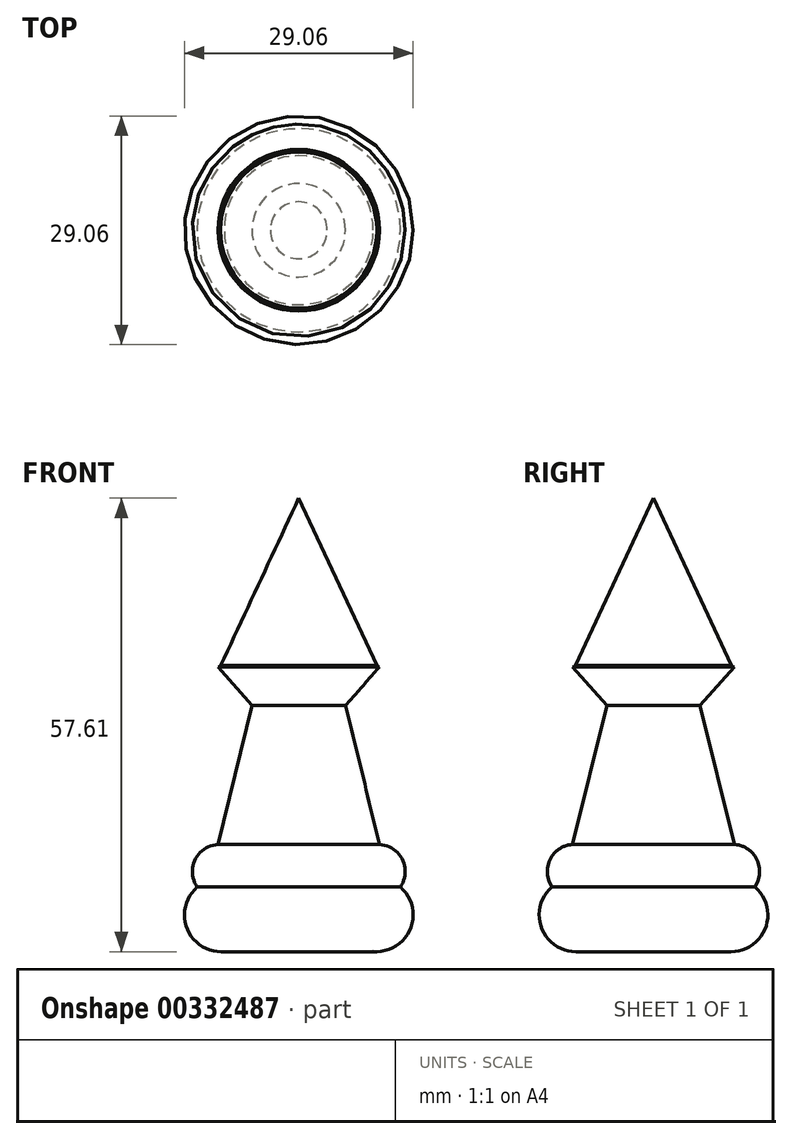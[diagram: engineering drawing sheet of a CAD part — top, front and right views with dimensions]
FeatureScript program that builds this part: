
annotation { "Feature Type Name" : "Feature", "Feature Type Description" : "" }
export const myFeature = defineFeature(function(context is Context, id is Id, definition is map)
    precondition{}
    {
        {
            var Q0;
            Q0=qCreatedBy(makeId("Front.planeOp"),FACE);
            var sketch = newSketch(context, id + "F0", { "sketchPlane" : qUnion([Q0])});
            skLineSegment(sketch, "E0", {"start": v(0, -70.9) * mm, "end": v(-10.27, -70.9) * mm});
            skCircle(sketch, "E1", {"center": v(-9.87, -66.25) * mm, "radius": 4.66 * mm});
            skPoint(sketch, "E1.second.point", {"position": v(-13.74, -63.66) * mm});
            skPoint(sketch, "E1.third.point", {"position": v(-7.09, -62.5) * mm});
            skCircle(sketch, "E2", {"center": v(-10.06, -60.74) * mm, "radius": 3.45 * mm});
            skPoint(sketch, "E2.second.point", {"position": v(-10.27, -57.3) * mm});
            skPoint(sketch, "E2.third.point", {"position": v(-12.88, -58.74) * mm});
            skLineSegment(sketch, "E3", {"start": v(-10.27, -57.3) * mm, "end": v(-5.93, -39.64) * mm});
            skLineSegment(sketch, "E4", {"start": v(-5.93, -39.64) * mm, "end": v(-10.27, -34.72) * mm});
            skLineSegment(sketch, "E5", {"start": v(-10.27, -34.72) * mm, "end": v(0, -34.72) * mm});
            skLineSegment(sketch, "E6", {"start": v(0, -34.72) * mm, "end": v(0, -70.9) * mm});
            skSolve(sketch);
        }
        {
            var Q0;
            {var subQ0=sQuery(id+"F0.wireOp",EDGE,"E1");var subQ1=sQuery(id+"F0.wireOp",EDGE,"E0");var subQ2=makeQuery(id+"F0.imprint","INTERSECT",VERTEX,{"disambiguationData":[OD(0.0)],"derivedFrom":[subQ1,subQ0]});Q0=makeQuery(id+"F0.imprint","IMPRINT",FACE,{"disambiguationData":[TD([[makeQuery(id+"F0.imprint","IMPRINT",EDGE,{"disambiguationData":[TD([[subQ2,1.0]])],"derivedFrom":subQ1}),1.0]])]});}
            var Q1;
            {var subQ0=sQuery(id+"F0.wireOp",EDGE,"E2");var subQ1=sQuery(id+"F0.wireOp",EDGE,"E1");var subQ2=makeQuery(id+"F0.imprint","INTERSECT",VERTEX,{"disambiguationData":[OD(0.0)],"derivedFrom":[subQ1,subQ0]});Q1=makeQuery(id+"F0.imprint","IMPRINT",FACE,{"disambiguationData":[TD([[makeQuery(id+"F0.imprint","IMPRINT",EDGE,{"disambiguationData":[TD([[subQ2,1.0]])],"derivedFrom":subQ1}),-1.0]])]});}
            var Q2;
            {var subQ0=sQuery(id+"F0.wireOp",EDGE,"E2");var subQ1=sQuery(id+"F0.wireOp",EDGE,"E1");var subQ2=makeQuery(id+"F0.imprint","INTERSECT",VERTEX,{"disambiguationData":[OD(0.0)],"derivedFrom":[subQ1,subQ0]});Q2=makeQuery(id+"F0.imprint","IMPRINT",FACE,{"disambiguationData":[TD([[makeQuery(id+"F0.imprint","IMPRINT",EDGE,{"disambiguationData":[TD([[subQ2,1.0]])],"derivedFrom":subQ1}),1.0]])]});}
            var Q3;
            {var subQ0=sQuery(id+"F0.wireOp",EDGE,"E1");var subQ1=sQuery(id+"F0.wireOp",EDGE,"E0");var subQ2=makeQuery(id+"F0.imprint","INTERSECT",VERTEX,{"disambiguationData":[OD(0.0)],"derivedFrom":[subQ1,subQ0]});Q3=makeQuery(id+"F0.imprint","IMPRINT",FACE,{"disambiguationData":[TD([[makeQuery(id+"F0.imprint","IMPRINT",EDGE,{"disambiguationData":[TD([[subQ2,1.0]])],"derivedFrom":subQ1}),-1.0]])]});}
            var Q4;
            {var subQ0=sQuery(id+"F0.wireOp",EDGE,"E3");Q4=makeQuery(id+"F0.imprint","IMPRINT",FACE,{"disambiguationData":[TD([[makeQuery(id+"F0.imprint","IMPRINT",EDGE,{"derivedFrom":subQ0}),-1.0]])]});}
            var Q5;
            Q5=sQuery(id+"F0.wireOp",EDGE,"E6");
            revolve(context, id + "F1", {"entities" : qUnion([Q0, Q1, Q2, Q3, Q4]), "axis" : qUnion([Q5]), "revolveType" : RevolveType.FULL});
        }
        {
            var Q0;
            Q0=qCreatedBy(makeId("Front.planeOp"),FACE);
            var sketch = newSketch(context, id + "F2", { "sketchPlane" : qUnion([Q0])});
            skLineSegment(sketch, "E7", {"start": v(-9.91, -34.59) * mm, "end": v(0, -13.3) * mm});
            skLineSegment(sketch, "E8", {"start": v(0, -13.3) * mm, "end": v(0, -34.8) * mm});
            skLineSegment(sketch, "E9", {"start": v(0, -34.8) * mm, "end": v(-9.91, -34.59) * mm});
            skSolve(sketch);
        }
        {
            var Q0;
            Q0=makeQuery(id+"F2.imprint","IMPRINT",FACE,{"disambiguationData":[TD([[makeQuery(id+"F2.imprint","IMPRINT",EDGE,{"derivedFrom":sQuery(id+"F2.wireOp",EDGE,"E7")}),-1.0]])]});
            var Q1;
            Q1=sQuery(id+"F2.wireOp",EDGE,"E8");
            revolve(context, id + "F3", {"operationType" : NewBodyOperationType.ADD, "entities" : qUnion([Q0]), "axis" : qUnion([Q1]), "revolveType" : RevolveType.FULL});
        }
    });
